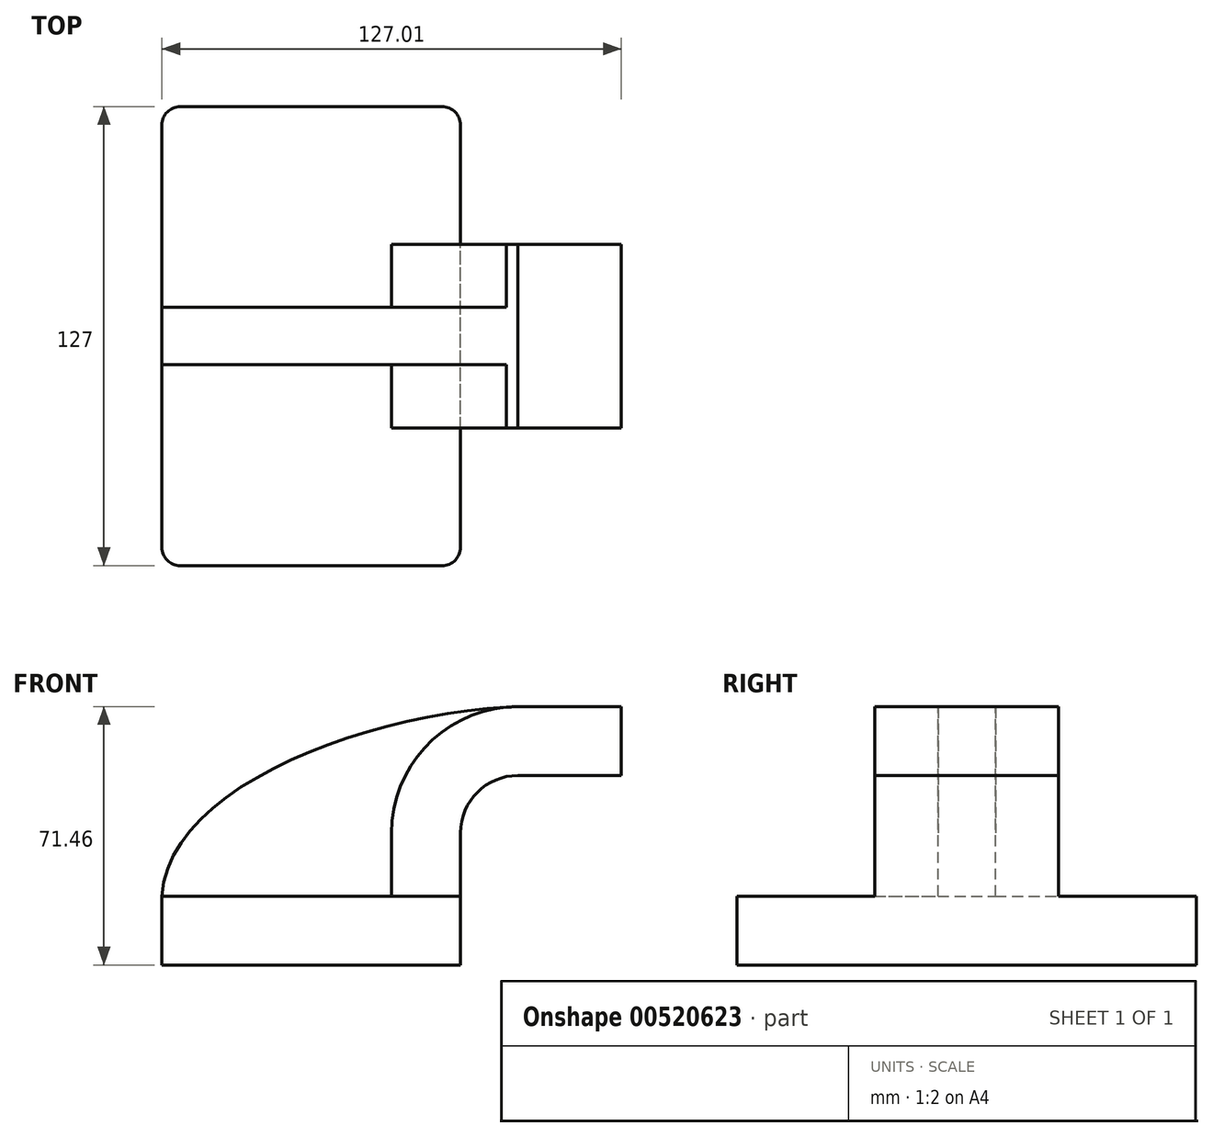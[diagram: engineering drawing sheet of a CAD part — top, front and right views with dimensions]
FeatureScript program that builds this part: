
annotation { "Feature Type Name" : "Feature", "Feature Type Description" : "" }
export const myFeature = defineFeature(function(context is Context, id is Id, definition is map)
    precondition{}
    {
        {
            var Q0;
            Q0=qCreatedBy(makeId("Front.planeOp"),FACE);
            var sketch = newSketch(context, id + "F0", { "sketchPlane" : qUnion([Q0])});
            skLineSegment(sketch, "E0.rect.bottom", {"start": v(-41.28, 9.52) * mm, "end": v(41.28, 9.52) * mm});
            skLineSegment(sketch, "E0.rect.top", {"start": v(-41.28, -9.52) * mm, "end": v(41.28, -9.52) * mm});
            skLineSegment(sketch, "E0.rect.left", {"start": v(-41.28, 9.52) * mm, "end": v(-41.28, -9.52) * mm});
            skLineSegment(sketch, "E0.rect.right", {"start": v(41.28, 9.52) * mm, "end": v(41.28, -9.52) * mm});
            skPoint(sketch, "E0.rect.middle", {"position": v(0, 0) * mm});
            skLineSegment(sketch, "E1", {"start": v(41.28, 9.52) * mm, "end": v(41.28, 27) * mm});
            skArc(sketch, "E2", {"start": v(41.28, 27) * mm, "mid": v(45.92, 38.23) * mm, "end": v(57.15, 42.88) * mm});
            skLineSegment(sketch, "E3", {"start": v(57.15, 42.88) * mm, "end": v(85.72, 42.88) * mm});
            skLineSegment(sketch, "E4.rect.bottom", {"start": v(60.32, 38.1) * mm, "end": v(111.12, 38.1) * mm});
            skLineSegment(sketch, "E4.rect.top", {"start": v(60.32, 66.68) * mm, "end": v(111.12, 66.68) * mm});
            skLineSegment(sketch, "E4.rect.left", {"start": v(60.32, 38.1) * mm, "end": v(60.32, 66.68) * mm});
            skLineSegment(sketch, "E4.rect.right", {"start": v(111.13, 38.1) * mm, "end": v(111.12, 66.68) * mm});
            skPoint(sketch, "E4.rect.middle", {"position": v(85.72, 52.39) * mm});
            skLineSegment(sketch, "E5.0", {"start": v(57.15, 61.93) * mm, "end": v(85.72, 61.93) * mm});
            skArc(sketch, "E5.1", {"start": v(22.23, 27) * mm, "mid": v(32.45, 51.7) * mm, "end": v(57.15, 61.93) * mm});
            skLineSegment(sketch, "E5.2", {"start": v(22.23, 9.52) * mm, "end": v(22.23, 27) * mm});
            skLineSegment(sketch, "E6", {"start": v(85.72, 38.1) * mm, "end": v(85.72, 66.68) * mm});
            skFitSpline(sketch, "E7", {"points": [v(-41.28, 9.53) * mm, v(57.15, 61.93) * mm], "startDerivative": vector(5.2, 92.34) * mm, "endDerivative": vector(120.92, 4.22) * mm});
            skSolve(sketch);
        }
        {
            var Q0;
            Q0=makeQuery(id+"F0.imprint","IMPRINT",FACE,{"disambiguationData":[TD([[makeQuery(id+"F0.imprint","IMPRINT",EDGE,{"derivedFrom":sQuery(id+"F0.wireOp",EDGE,"E0.rect.top")}),1.0]])]});
            extrude(context, id + "F1", {"entities" : qUnion([Q0]), "endBound" : BoundingType.SYMMETRIC, "depth" : 127 * mm, "offsetDistance" : 25.4 * mm});
        }
        {
            var Q0;
            {var subQ9=sQuery(id+"F0.wireOp",EDGE,"E1");Q0=makeQuery(id+"F0.imprint","IMPRINT",FACE,{"disambiguationData":[TD([[makeQuery(id+"F0.imprint","IMPRINT",EDGE,{"derivedFrom":subQ9}),1.0]])]});}
            var Q1;
            {var subQ0=sQuery(id+"F0.wireOp",EDGE,"E6");var subQ1=sQuery(id+"F0.wireOp",EDGE,"E3");var subQ2=makeQuery(id+"F0.imprint","INTERSECT",VERTEX,{"derivedFrom":[subQ1,subQ0]});Q1=makeQuery(id+"F0.imprint","IMPRINT",FACE,{"disambiguationData":[TD([[makeQuery(id+"F0.imprint","IMPRINT",EDGE,{"disambiguationData":[TD([[subQ2,1.0]])],"derivedFrom":subQ1}),1.0]])]});}
            extrude(context, id + "F2", {"entities" : qUnion([Q0, Q1]), "operationType" : NewBodyOperationType.ADD, "endBound" : BoundingType.SYMMETRIC, "depth" : 50.8 * mm, "offsetDistance" : 25.4 * mm});
        }
        {
            var Q0;
            {var subQ3=sQuery(id+"F0.wireOp",EDGE,"E5.2");Q0=makeQuery(id+"F0.imprint","IMPRINT",FACE,{"disambiguationData":[TD([[makeQuery(id+"F0.imprint","IMPRINT",EDGE,{"derivedFrom":subQ3}),1.0]])]});}
            extrude(context, id + "F3", {"entities" : qUnion([Q0]), "operationType" : NewBodyOperationType.ADD, "endBound" : BoundingType.SYMMETRIC, "depth" : 15.88 * mm, "offsetDistance" : 25.4 * mm});
        }
        {
            var Q0;
            Q0=makeQuery(id+"F1.opExtrude","CAP_EDGE",EDGE,{"disambiguationData":[OSD([sQuery(id+"F0.wireOp",EDGE,"E0.rect.right")])],"isStart":false});
            var Q1;
            Q1=makeQuery(id+"F1.opExtrude","CAP_EDGE",EDGE,{"disambiguationData":[OSD([sQuery(id+"F0.wireOp",EDGE,"E0.rect.left")])],"isStart":false});
            var Q2;
            Q2=makeQuery(id+"F1.opExtrude","CAP_EDGE",EDGE,{"disambiguationData":[OSD([sQuery(id+"F0.wireOp",EDGE,"E0.rect.right")])],"isStart":true});
            var Q3;
            Q3=makeQuery(id+"F1.opExtrude","CAP_EDGE",EDGE,{"disambiguationData":[OSD([sQuery(id+"F0.wireOp",EDGE,"E0.rect.left")])],"isStart":true});
            fillet(context, id + "F4", {"entities" : qUnion([Q0, Q1, Q2, Q3]), "radius" : 5.08 * mm, "tangentPropagation" : true, "allowEdgeOverflow" : false});
        }
    });
